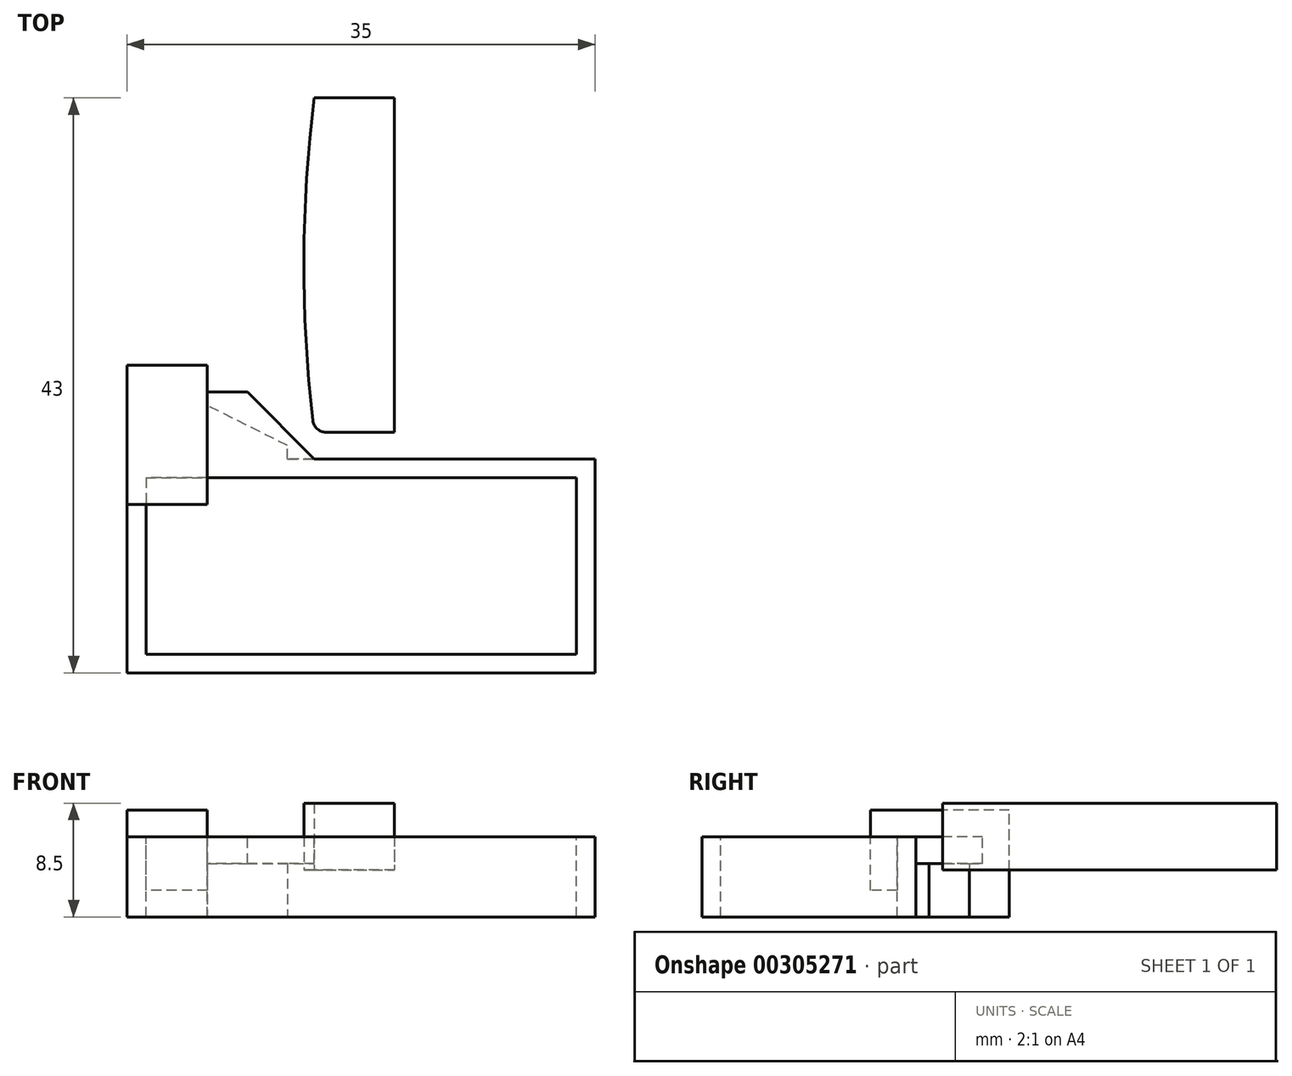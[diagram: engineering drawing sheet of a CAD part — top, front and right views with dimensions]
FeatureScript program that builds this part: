
annotation { "Feature Type Name" : "Feature", "Feature Type Description" : "" }
export const myFeature = defineFeature(function(context is Context, id is Id, definition is map)
    precondition{}
    {
        {
            var Q0;
            Q0=qCreatedBy(makeId("Top.planeOp"),FACE);
            var sketch = newSketch(context, id + "F0", { "sketchPlane" : qUnion([Q0])});
            skLineSegment(sketch, "E0.bottom", {"start": v(14, 0) * mm, "end": v(35, 0) * mm});
            skLineSegment(sketch, "E0.top", {"start": v(0, -16) * mm, "end": v(35, -16) * mm});
            skLineSegment(sketch, "E0.left", {"start": v(0, 0) * mm, "end": v(0, -16) * mm});
            skLineSegment(sketch, "E0.right", {"start": v(35, 0) * mm, "end": v(35, -16) * mm});
            skLineSegment(sketch, "E1.0", {"start": v(1.4, -1.4) * mm, "end": v(33.6, -1.4) * mm});
            skLineSegment(sketch, "E1.1", {"start": v(1.4, -1.4) * mm, "end": v(1.4, -14.6) * mm});
            skLineSegment(sketch, "E1.2", {"start": v(1.4, -14.6) * mm, "end": v(33.6, -14.6) * mm});
            skLineSegment(sketch, "E1.3", {"start": v(33.6, -1.4) * mm, "end": v(33.6, -14.6) * mm});
            skLineSegment(sketch, "E2", {"start": v(0, 0) * mm, "end": v(0, 5) * mm});
            skLineSegment(sketch, "E3", {"start": v(0, 5) * mm, "end": v(9, 5) * mm});
            skLineSegment(sketch, "E4", {"start": v(9, 5) * mm, "end": v(14, 0) * mm});
            skLineSegment(sketch, "E5", {"start": v(14, 0) * mm, "end": v(0, 0) * mm});
            skSolve(sketch);
        }
        {
            var Q0;
            Q0=makeQuery(id+"F0.imprint","IMPRINT",FACE,{"disambiguationData":[TD([[makeQuery(id+"F0.imprint","IMPRINT",EDGE,{"derivedFrom":sQuery(id+"F0.wireOp",EDGE,"E0.bottom")}),-1.0]])]});
            extrude(context, id + "F1", {"entities" : qUnion([Q0]), "oppositeDirection" : true, "depth" : 6 * mm});
        }
        {
            var Q0;
            Q0=makeQuery(id+"F0.imprint","IMPRINT",FACE,{"disambiguationData":[TD([[makeQuery(id+"F0.imprint","IMPRINT",EDGE,{"derivedFrom":sQuery(id+"F0.wireOp",EDGE,"E2")}),-1.0]])]});
            extrude(context, id + "F2", {"entities" : qUnion([Q0]), "operationType" : NewBodyOperationType.ADD, "oppositeDirection" : true, "depth" : 2 * mm});
        }
        {
            var Q0;
            Q0=makeQuery(id+"F2.boolean.opBoolean","MERGE",FACE,{"derivedFrom":[makeQuery(id+"F1.opExtrude","SWEPT_FACE",FACE,{"disambiguationData":[OSD([sQuery(id+"F0.wireOp",EDGE,"E0.left")])]}),makeQuery(id+"F2.opExtrude","SWEPT_FACE",FACE,{"disambiguationData":[OSD([sQuery(id+"F0.wireOp",EDGE,"E2")])]})]});
            var sketch = newSketch(context, id + "F3", { "sketchPlane" : qUnion([Q0])});
            skLineSegment(sketch, "E6.0", {"start": v(0, 0) * mm, "end": v(-5, 0) * mm});
            skLineSegment(sketch, "E7.0", {"start": v(0, 0) * mm, "end": v(1.4, 0) * mm});
            skLineSegment(sketch, "E8.0", {"start": v(-5, -2) * mm, "end": v(-5, 0) * mm});
            skLineSegment(sketch, "E9.0", {"start": v(0, -2) * mm, "end": v(-5, -2) * mm});
            skLineSegment(sketch, "E10.0", {"start": v(0, -6) * mm, "end": v(0, -2) * mm});
            skPoint(sketch, "E11.orphan", {"position": v(16, 0) * mm});
            skPoint(sketch, "E12.orphan", {"position": v(16, -6) * mm});
            skLineSegment(sketch, "E13.2", {"start": v(0, 2) * mm, "end": v(3.4, 2) * mm});
            skLineSegment(sketch, "E13.3", {"start": v(0, 2) * mm, "end": v(-7, 2) * mm});
            skLineSegment(sketch, "E13.4", {"start": v(-7, -6) * mm, "end": v(-7, 2) * mm});
            skPoint(sketch, "E14.0.start.orphan", {"position": v(0, -6) * mm});
            skPoint(sketch, "E15.0.start.orphan", {"position": v(1.4, -6) * mm});
            skLineSegment(sketch, "E16", {"start": v(1.4, 0) * mm, "end": v(1.4, -4) * mm});
            skLineSegment(sketch, "E17", {"start": v(1.4, -4) * mm, "end": v(3.4, -4) * mm});
            skLineSegment(sketch, "E18", {"start": v(3.4, -4) * mm, "end": v(3.4, 2) * mm});
            skPoint(sketch, "E19.orphan", {"position": v(0, -4) * mm});
            skLineSegment(sketch, "E20", {"start": v(0, -6) * mm, "end": v(-7, -6) * mm});
            skSolve(sketch);
        }
        {
            var Q0;
            Q0=makeQuery(id+"F3.imprint","IMPRINT",FACE,{"disambiguationData":[TD([[makeQuery(id+"F3.imprint","IMPRINT",EDGE,{"derivedFrom":sQuery(id+"F3.wireOp",EDGE,"E6.0")}),1.0]])]});
            var Q1;
            {var subQ0=sQuery(id+"F3.wireOp",EDGE,"E16");Q1=makeQuery(id+"F3.imprint","IMPRINT",FACE,{"disambiguationData":[TD([[makeQuery(id+"F3.imprint","IMPRINT",EDGE,{"derivedFrom":subQ0}),1.0]])]});}
            extrude(context, id + "F4", {"entities" : qUnion([Q0, Q1]), "oppositeDirection" : true, "depth" : 6 * mm});
        }
        {
            var Q0;
            Q0=makeQuery(id+"F4.opExtrude","SWEPT_FACE",FACE,{"disambiguationData":[OSD([sQuery(id+"F3.wireOp",EDGE,"E20")])]});
            var sketch = newSketch(context, id + "F5", { "sketchPlane" : qUnion([Q0])});
            skLineSegment(sketch, "E21.0", {"start": v(6, 0) * mm, "end": v(6, -4) * mm});
            skLineSegment(sketch, "E22.0", {"start": v(6, 0) * mm, "end": v(12, 0) * mm});
            skPoint(sketch, "E23.orphan", {"position": v(0, 0) * mm});
            skLineSegment(sketch, "E24", {"start": v(12, 0) * mm, "end": v(12, -1) * mm});
            skLineSegment(sketch, "E25", {"start": v(12, -1) * mm, "end": v(6, -4) * mm});
            skSolve(sketch);
        }
        {
            var Q0;
            Q0=makeQuery(id+"F5.imprint","IMPRINT",FACE,{"disambiguationData":[TD([[makeQuery(id+"F5.imprint","IMPRINT",EDGE,{"derivedFrom":sQuery(id+"F5.wireOp",EDGE,"E21.0")}),1.0]])]});
            var Q1;
            Q1=makeQuery(id+"F2.opExtrude","CAP_FACE",FACE,{"disambiguationData":[OSD([sQuery(id+"F0.wireOp",EDGE,"E2"),sQuery(id+"F0.wireOp",EDGE,"E3"),sQuery(id+"F0.wireOp",EDGE,"E4"),sQuery(id+"F0.wireOp",EDGE,"E5")])],"isStart":false});
            extrude(context, id + "F6", {"entities" : qUnion([Q0]), "operationType" : NewBodyOperationType.ADD, "endBound" : BoundingType.UP_TO_SURFACE, "oppositeDirection" : true, "endBoundEntityFace" : qUnion([Q1]), "depth" : 25 * mm});
        }
        {
            var Q0;
            {var subQ0=sQuery(id+"F0.wireOp",EDGE,"E5");Q0=makeQuery(id+"F2.boolean.opBoolean","MERGE",FACE,{"derivedFrom":[makeQuery(id+"F1.opExtrude","CAP_FACE",FACE,{"disambiguationData":[OSD([sQuery(id+"F0.wireOp",EDGE,"E0.bottom"),sQuery(id+"F0.wireOp",EDGE,"E0.top"),sQuery(id+"F0.wireOp",EDGE,"E0.left"),sQuery(id+"F0.wireOp",EDGE,"E0.right"),sQuery(id+"F0.wireOp",EDGE,"E1.0"),sQuery(id+"F0.wireOp",EDGE,"E1.1"),sQuery(id+"F0.wireOp",EDGE,"E1.2"),sQuery(id+"F0.wireOp",EDGE,"E1.3"),subQ0])],"isStart":true}),makeQuery(id+"F2.opExtrude","CAP_FACE",FACE,{"disambiguationData":[OSD([sQuery(id+"F0.wireOp",EDGE,"E2"),sQuery(id+"F0.wireOp",EDGE,"E3"),sQuery(id+"F0.wireOp",EDGE,"E4"),subQ0])],"isStart":true})]});}
            var sketch = newSketch(context, id + "F7", { "sketchPlane" : qUnion([Q0])});
            skPoint(sketch, "E26.0", {"position": v(14, 0) * mm});
            skLineSegment(sketch, "E27", {"start": v(14, 0) * mm, "end": v(14, 2) * mm, "construction": true});
            skLineSegment(sketch, "E28", {"start": v(14, 2) * mm, "end": v(20, 2) * mm});
            skLineSegment(sketch, "E29", {"start": v(14, 2) * mm, "end": v(14, 27) * mm, "construction": true});
            skArc(sketch, "E30", {"start": v(14, 27) * mm, "mid": v(13.22, 14.5) * mm, "end": v(14, 2) * mm});
            skLineSegment(sketch, "E31", {"start": v(20, 2) * mm, "end": v(20, 27) * mm});
            skLineSegment(sketch, "E32", {"start": v(20, 27) * mm, "end": v(14, 27) * mm});
            skSolve(sketch);
        }
        {
            var Q0;
            Q0=makeQuery(id+"F7.imprint","IMPRINT",FACE,{"disambiguationData":[TD([[makeQuery(id+"F7.imprint","IMPRINT",EDGE,{"derivedFrom":sQuery(id+"F7.wireOp",EDGE,"E28")}),1.0]])]});
            extrude(context, id + "F8", {"entities" : qUnion([Q0]), "endBound" : BoundingType.SYMMETRIC, "depth" : 5 * mm});
        }
        {
            var Q0;
            Q0=makeQuery(id+"F8.opExtrude","SWEPT_EDGE",EDGE,{"disambiguationData":[OSD([sQuery(id+"F7.wireOp",EDGE,"E28"),sQuery(id+"F7.wireOp",EDGE,"E30")])]});
            fillet(context, id + "F9", {"entities" : qUnion([Q0]), "radius" : 1 * mm, "tangentPropagation" : true, "allowEdgeOverflow" : false});
        }
    });
